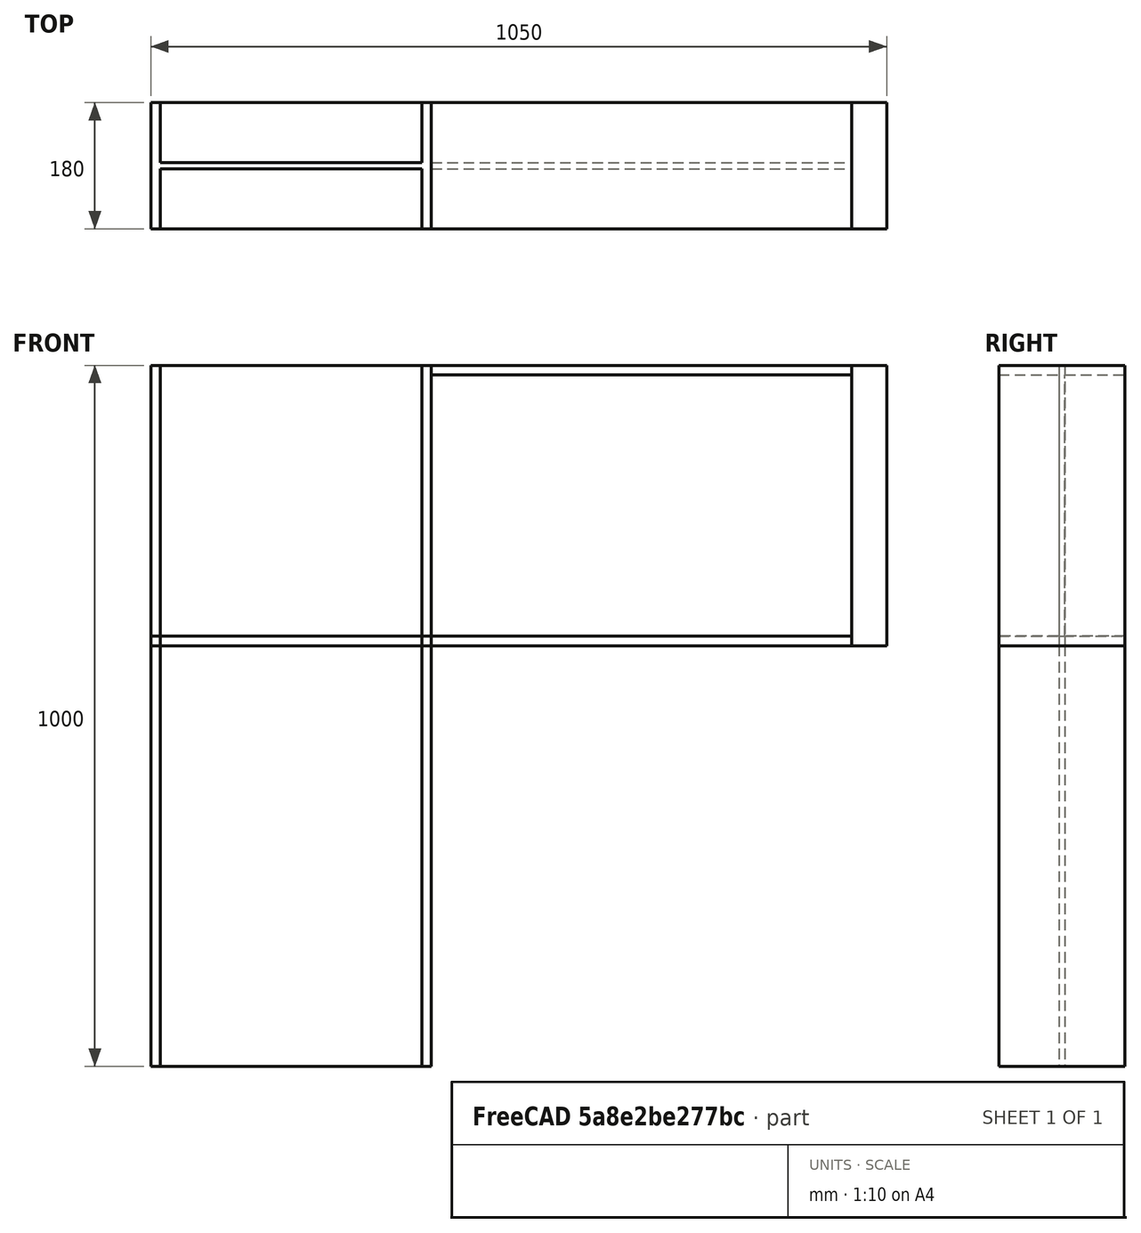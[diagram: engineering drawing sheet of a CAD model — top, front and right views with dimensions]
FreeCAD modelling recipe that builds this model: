
FCSTD DOCUMENT  (FreeCAD 0.21R33771 (Git))
Label: IPE400_4
License: All rights reserved
LicenseURL: http://en.wikipedia.org/wiki/All_rights_reserved
objects: Sketcher::SketchObject×2, Part::Extrusion×2, Part::Box×2, Fem::ConstraintForce×2, Fem::ConstraintFixed×1, App::MaterialObjectPython×1, Fem::FemSolverObjectPython×1, Fem::ConstraintDisplacement×1, Part::FeaturePython×1, Fem::FemMeshObjectPython×1, Fem::FemAnalysis×1
note: 7 computed .brp shape members not serialized (recipe doc carries the construction recipe); baked Part::Feature solids carry a one-line shape summary decoded from their .brp

FEATURE [Sketcher::SketchObject] Sketch
  FullyConstrained = true
  Placement = pos=(0,0,0) rot=(0.57735,0.57735,0.57735;2.0944rad)
  sketch-geometry (12):
    g0: LineSegment StartX=0 StartY=0 StartZ=0 EndX=180 EndY=0 EndZ=0
    g1: LineSegment StartX=180 StartY=0 StartZ=0 EndX=180 EndY=13.5 EndZ=0
    g2: LineSegment StartX=180 StartY=13.5 StartZ=0 EndX=94.3 EndY=13.5 EndZ=0
    g3: LineSegment StartX=94.3 StartY=13.5 StartZ=0 EndX=94.3 EndY=386.5 EndZ=0
    g4: LineSegment StartX=94.3 StartY=386.5 StartZ=0 EndX=180 EndY=386.5 EndZ=0
    g5: LineSegment StartX=180 StartY=386.5 StartZ=0 EndX=180 EndY=400 EndZ=0
    g6: LineSegment StartX=180 StartY=400 StartZ=0 EndX=0 EndY=400 EndZ=0
    g7: LineSegment StartX=0 StartY=400 StartZ=0 EndX=0 EndY=386.5 EndZ=0
    g8: LineSegment StartX=0 StartY=386.5 StartZ=0 EndX=85.7 EndY=386.5 EndZ=0
    g9: LineSegment StartX=85.7 StartY=386.5 StartZ=0 EndX=85.7 EndY=13.5 EndZ=0
    g10: LineSegment StartX=85.7 StartY=13.5 StartZ=0 EndX=0 EndY=13.5 EndZ=0
    g11: LineSegment StartX=0 StartY=13.5 StartZ=0 EndX=0 EndY=0 EndZ=0
  constraints (35):
    c: Coincident(g-1,g0)
    c: PointOnObject(g0,g-1)
    c: Coincident(g0,g1)
    c: Vertical(g1)
    c: Coincident(g1,g2)
    c: Horizontal(g2)
    c: Coincident(g2,g3)
    c: Vertical(g3)
    c: Coincident(g3,g4)
    c: Horizontal(g4)
    c: Coincident(g4,g5)
    c: Vertical(g5)
    c: Coincident(g5,g6)
    c: Horizontal(g6)
    c: Coincident(g6,g7)
    c: Vertical(g7)
    c: Coincident(g7,g8)
    c: Horizontal(g8)
    c: Coincident(g8,g9)
    c: Vertical(g9)
    c: Coincident(g9,g10)
    c: Horizontal(g10)
    c: Coincident(g10,g11)
    c: Coincident(g11,g0)
    c: DistanceX(g0,g0) = 180
    c: DistanceX(g6,g6) = 180
    c: PointOnObject(g6,g-2)
    c: Vertical(g11)
    c: DistanceX(g2,g2) = 85.7
    c: Equal(g10,g2)
    c: DistanceY(g11,g11) = 13.5
    c: Equal(g11,g1)
    c: Equal(g11,g7)
    c: Equal(g11,g5)
    c: DistanceY(g0,g6) = 400
FEATURE [Part::Extrusion] Extrude
  Base = -> Sketch
  Dir = (1,0,0)
  DirMode = 2
  FaceMakerClass = Part::FaceMakerBullseye
  LengthFwd = 600
  LengthRev = 0
  Solid = true
  Symmetric = false
FEATURE [Sketcher::SketchObject] Sketch001
  FullyConstrained = true
  Placement = pos=(0,0,0) rot=(0.57735,0.57735,0.57735;2.0944rad)
  sketch-geometry (12):
    g0: LineSegment StartX=0 StartY=0 StartZ=0 EndX=180 EndY=0 EndZ=0
    g1: LineSegment StartX=180 StartY=0 StartZ=0 EndX=180 EndY=13.5 EndZ=0
    g2: LineSegment StartX=180 StartY=13.5 StartZ=0 EndX=94.3 EndY=13.5 EndZ=0
    g3: LineSegment StartX=94.3 StartY=13.5 StartZ=0 EndX=94.3 EndY=386.5 EndZ=0
    g4: LineSegment StartX=94.3 StartY=386.5 StartZ=0 EndX=180 EndY=386.5 EndZ=0
    g5: LineSegment StartX=180 StartY=386.5 StartZ=0 EndX=180 EndY=400 EndZ=0
    g6: LineSegment StartX=180 StartY=400 StartZ=0 EndX=0 EndY=400 EndZ=0
    g7: LineSegment StartX=0 StartY=400 StartZ=0 EndX=0 EndY=386.5 EndZ=0
    g8: LineSegment StartX=0 StartY=386.5 StartZ=0 EndX=85.7 EndY=386.5 EndZ=0
    g9: LineSegment StartX=85.7 StartY=386.5 StartZ=0 EndX=85.7 EndY=13.5 EndZ=0
    g10: LineSegment StartX=85.7 StartY=13.5 StartZ=0 EndX=0 EndY=13.5 EndZ=0
    g11: LineSegment StartX=0 StartY=13.5 StartZ=0 EndX=0 EndY=0 EndZ=0
  constraints (35):
    c: Coincident(g-1,g0)
    c: PointOnObject(g0,g-1)
    c: Coincident(g0,g1)
    c: Vertical(g1)
    c: Coincident(g1,g2)
    c: Horizontal(g2)
    c: Coincident(g2,g3)
    c: Vertical(g3)
    c: Coincident(g3,g4)
    c: Horizontal(g4)
    c: Coincident(g4,g5)
    c: Vertical(g5)
    c: Coincident(g5,g6)
    c: Horizontal(g6)
    c: Coincident(g6,g7)
    c: Vertical(g7)
    c: Coincident(g7,g8)
    c: Horizontal(g8)
    c: Coincident(g8,g9)
    c: Vertical(g9)
    c: Coincident(g9,g10)
    c: Horizontal(g10)
    c: Coincident(g10,g11)
    c: Coincident(g11,g0)
    c: DistanceX(g0,g0) = 180
    c: DistanceX(g6,g6) = 180
    c: PointOnObject(g6,g-2)
    c: Vertical(g11)
    c: DistanceX(g2,g2) = 85.7
    c: Equal(g10,g2)
    c: DistanceY(g11,g11) = 13.5
    c: Equal(g11,g1)
    c: Equal(g11,g7)
    c: Equal(g11,g5)
    c: DistanceY(g0,g6) = 400
FEATURE [Part::Extrusion] Extrude001
  Base = -> Sketch001
  Dir = (1,0,0)
  DirMode = 2
  FaceMakerClass = Part::FaceMakerBullseye
  LengthFwd = 1000
  LengthRev = 0
  Placement = pos=(-400,0,400) rot=(0,1,0;1.5708rad)
  Solid = true
  Symmetric = false
FEATURE [Part::Box] Box  label="Cube"
  AttacherType = Attacher::AttachEngine3D
  Height = 400
  Length = 50
  Placement = pos=(600,0,0) rot=(0,0,1;0rad)
  Width = 180
FEATURE [Fem::ConstraintForce] ConstraintForce
  Direction = -> Box [Edge12]
  DirectionVector = (1,0,0)
  Force = 1000000
  NormalDirection = (0,0,1)
  Points = (16) [(600,0,400),(616.667,0,400),(633.333,0,400),(650,0,400),(600,60,400),(616.667,60,400),(633.333,60,400),(650,60,400),(600,120,400),(616.667,120,400),+6 more]
  References = -> [Box]
  Scale = 11
FEATURE [Fem::ConstraintFixed] ConstraintFixed
  NormalDirection = (0,0,-1)
  Normals = (8) [(0,0,-1),(0,0,-1),(0,0,-1),(0,0,-1),(0,0,-1),(0,0,-1),(0,0,-1),(0,0,-1)]
  Points = (8) [(-400,180,-600),(0,180,-600),(-400,120,-600),(0,120,-600),(-400,60,-600),(0,60,-600),(-400,0,-600),(0,0,-600)]
  References = -> [Extrude001]
  Scale = 18
FEATURE [App::MaterialObjectPython] MaterialSolid  # material (typed FeaturePython)
  Category = 0
  Material = AuthorAndLicense=(c) 2014 M. Münch - GNU Lesser General Public License (LGPL),CardName=Steel-15CrNi6,Density=7800 kg/m^3,+16 more (map truncated)
FEATURE [Fem::ConstraintForce] ConstraintForce001
  Direction = -> Box [Edge9]
  DirectionVector = (-1,0,0)
  Force = 1000000
  NormalDirection = (0,0,-1)
  Points = (16) [(600,0,0),(616.667,0,0),(633.333,0,0),(650,0,0),(600,60,0),(616.667,60,0),(633.333,60,0),(650,60,0),(600,120,0),(616.667,120,0),(633.333,120,0),+5 more]
  References = -> [Box]
  Reversed = true
  Scale = 11
FEATURE [Fem::FemSolverObjectPython] SolverCcxTools  # FEM object (typed FeaturePython)
  AnalysisType = 0
  BeamShellResultOutput3D = false
  BucklingFactors = 1
  EigenmodeHighLimit = 1000000
  EigenmodeLowLimit = 0
  EigenmodesCount = 10
  GeometricalNonlinearity = 0
  IterationsControlParameterCutb = 0.25,0.5,0.75,0.85,,,1.5,
  IterationsControlParameterIter = 4,8,9,200,10,400,,200,,
  IterationsControlParameterTimeUse = false
  IterationsThermoMechMaximum = 2000
  IterationsUserDefinedIncrementations = false
  IterationsUserDefinedTimeStepLength = false
  MaterialNonlinearity = 0
  MatrixSolverType = 0
  SplitInputWriter = false
  ThermoMechSteadyState = true
  TimeEnd = 1
  TimeInitialStep = 0.01
FEATURE [Fem::ConstraintDisplacement] ConstraintDisplacement
  NormalDirection = (0,1,0)
  Normals = (16) [(0,1,0),(0,1,0),(0,1,0),(0,1,0),(0,1,0),(0,1,0),(0,1,0),(0,1,0),(0,1,0),(0,1,0),(0,1,0),(0,1,0),(0,1,0),(0,1,0),(0,1,0),(0,1,0)]
  Points = (16) [(600,180,0),(600,180,133.333),(600,180,266.667),(600,180,400),(616.667,180,0),(616.667,180,133.333),(616.667,180,266.667),(616.667,180,400),+8 more]
  References = -> [Box]
  Scale = 16
  hasXFormula = false
  hasYFormula = false
  hasZFormula = false
  rotxFix = false
  rotxFree = true
  rotyFix = false
  rotyFree = true
  rotzFix = false
  rotzFree = true
  useFlowSurfaceForce = false
  xDisplacement = 0
  xFix = false
  xFree = true
  xRotation = 0
  yDisplacement = 0
  yFix = false
  yFree = false
  yRotation = 0
  zDisplacement = 0
  zFix = false
  zFree = true
  zRotation = 0
FEATURE [Part::Box] Box002  label="Cube002"
  AttacherType = Attacher::AttachEngine3D
  Height = 13.5
  Length = 400
  Placement = pos=(-400,0,0) rot=(0,0,1;0rad)
  Width = 180
FEATURE [Part::FeaturePython] BooleanFragments  # WARN: FeaturePython — macro-defined, semantics opaque (R4)
  Mode = 2
  Objects = -> [Extrude,Extrude001,Box,Box002]
  Tolerance = 0
FEATURE [Fem::FemMeshObjectPython] FEMMeshGmsh  # FEM object (typed FeaturePython)
  Algorithm2D = 0
  Algorithm3D = 0
  CharacteristicLengthMax = 25
  CharacteristicLengthMin = 0
  CoherenceMesh = true
  ElementDimension = 0
  ElementOrder = 1
  GeometryTolerance = 1e-06
  GroupsOfNodes = false
  HighOrderOptimize = 0
  MeshSizeFromCurvature = 12
  OptimizeNetgen = false
  OptimizeStd = true
  Part = -> BooleanFragments
  RecombinationAlgorithm = 0
  Recombine3DAll = false
  RecombineAll = false
  SecondOrderLinear = false
FEATURE [Fem::FemAnalysis] Analysis
  Group = -> [ConstraintForce,ConstraintFixed,MaterialSolid,ConstraintForce001,SolverCcxTools,ConstraintDisplacement,FEMMeshGmsh]
